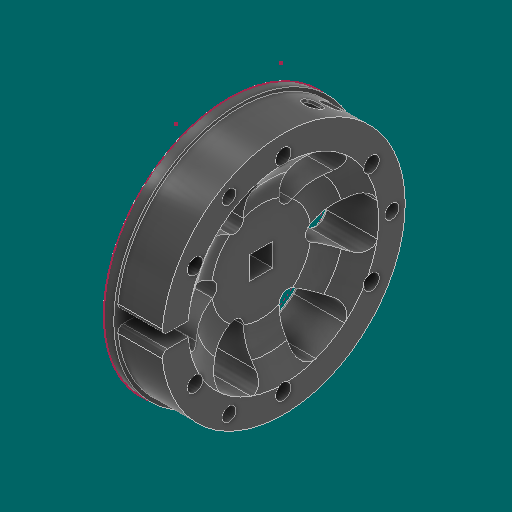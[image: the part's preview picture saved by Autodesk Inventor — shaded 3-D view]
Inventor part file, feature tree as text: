
AUTODESK INVENTOR PART (.ipt)
format: ipt  version: 2023.1 (Build 271208000, 208)  size: 568,832 bytes
history: native  units: in
note: dims shown in document units (in); Inventor stores cm internally (conversion verified against a paired STEP export)
features: sketch x5, other x3
ambient origin geometry x8: Origin, YZ Plane, XZ Plane, XY Plane, X Axis, Y Axis, Z Axis, Center Point
bodies: Solid1 (feature_tree)
feature tree (8):
  other  "WheelHalf_MIR.ipt"
  other  "Solid1::WheelHalf_MIR.ipt"
  other  "TaggingFeature1"
  sketch  "Sketch1"  dims[d0=0.3937in]
  sketch  "Sketch2"
  sketch  "Sketch3"
  sketch  "Sketch4"
  sketch  "Sketch5"
